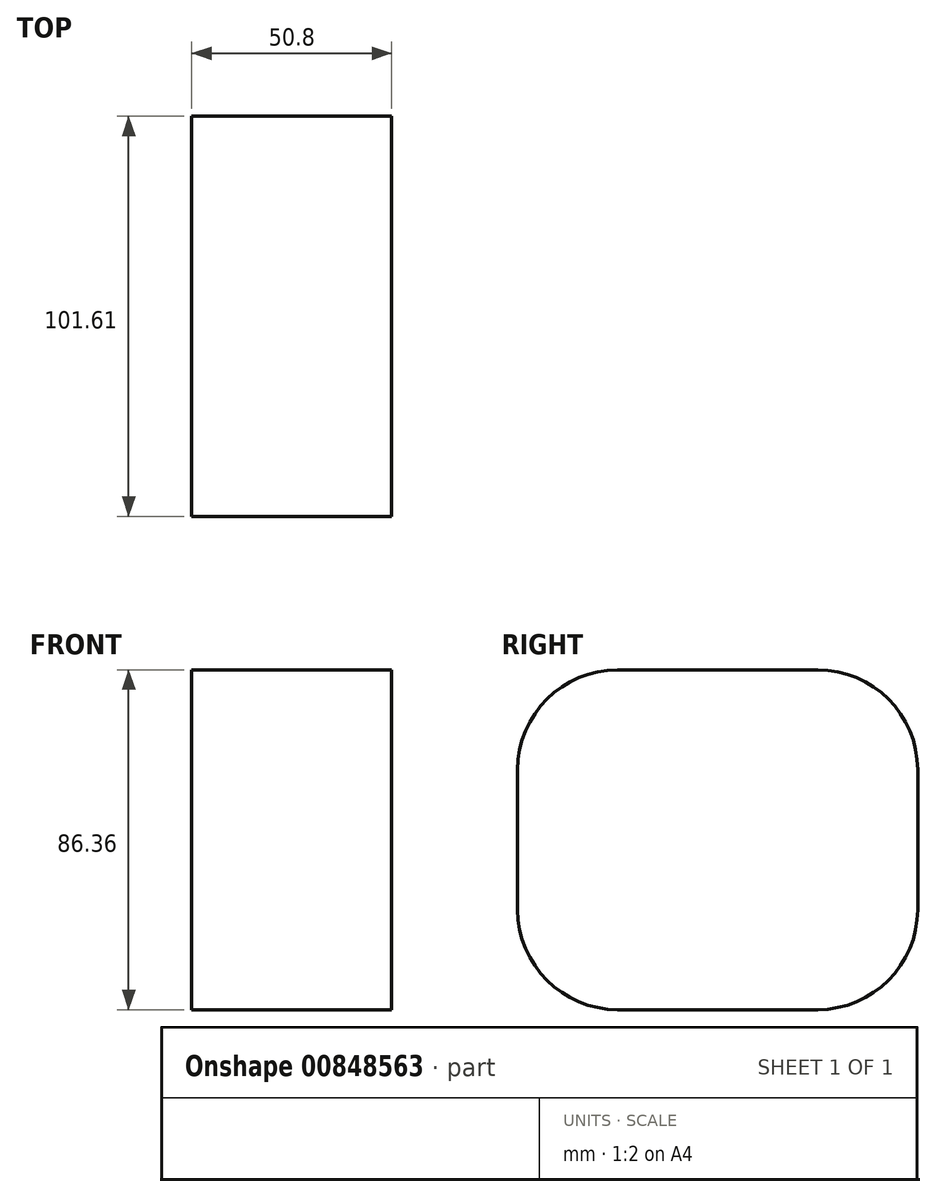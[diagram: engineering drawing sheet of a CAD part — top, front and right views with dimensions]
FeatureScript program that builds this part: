
annotation { "Feature Type Name" : "Feature", "Feature Type Description" : "" }
export const myFeature = defineFeature(function(context is Context, id is Id, definition is map)
    precondition{}
    {
        {
            var Q0;
            Q0=qCreatedBy(makeId("Right.planeOp"),FACE);
            var sketch = newSketch(context, id + "F0", { "sketchPlane" : qUnion([Q0])});
            skLineSegment(sketch, "E0.bottom", {"start": v(-51.83, 43.7) * mm, "end": v(49.78, 43.7) * mm});
            skLineSegment(sketch, "E0.top", {"start": v(-51.83, -42.67) * mm, "end": v(49.78, -42.67) * mm});
            skLineSegment(sketch, "E0.left", {"start": v(-51.83, 43.7) * mm, "end": v(-51.83, -42.67) * mm});
            skLineSegment(sketch, "E0.right", {"start": v(49.78, 43.7) * mm, "end": v(49.78, -42.67) * mm});
            skSolve(sketch);
        }
        {
            var Q0;
            Q0 = qSketchRegion(id + "F0", true);
            extrude(context, id + "F1", {"entities" : qUnion([Q0]), "depth" : 50.8 * mm, "offsetDistance" : 25.4 * mm});
        }
        {
            var Q0;
            Q0=makeQuery(id+"F1.opExtrude","SWEPT_EDGE",EDGE,{"disambiguationData":[OSD([sQuery(id+"F0.wireOp",EDGE,"E0.bottom"),sQuery(id+"F0.wireOp",EDGE,"E0.left")])]});
            fillet(context, id + "F2", {"entities" : qUnion([Q0]), "radius" : 25.4 * mm, "tangentPropagation" : true, "allowEdgeOverflow" : false});
        }
        {
            var Q0;
            Q0=makeQuery(id+"F1.opExtrude","SWEPT_EDGE",EDGE,{"disambiguationData":[OSD([sQuery(id+"F0.wireOp",EDGE,"E0.bottom"),sQuery(id+"F0.wireOp",EDGE,"E0.right")])]});
            var Q1;
            Q1=makeQuery(id+"F1.opExtrude","SWEPT_EDGE",EDGE,{"disambiguationData":[OSD([sQuery(id+"F0.wireOp",EDGE,"E0.top"),sQuery(id+"F0.wireOp",EDGE,"E0.left")])]});
            var Q2;
            Q2=makeQuery(id+"F1.opExtrude","SWEPT_EDGE",EDGE,{"disambiguationData":[OSD([sQuery(id+"F0.wireOp",EDGE,"E0.top"),sQuery(id+"F0.wireOp",EDGE,"E0.right")])]});
            fillet(context, id + "F3", {"entities" : qUnion([Q0, Q1, Q2]), "radius" : 25.4 * mm, "tangentPropagation" : true, "allowEdgeOverflow" : false});
        }
    });
